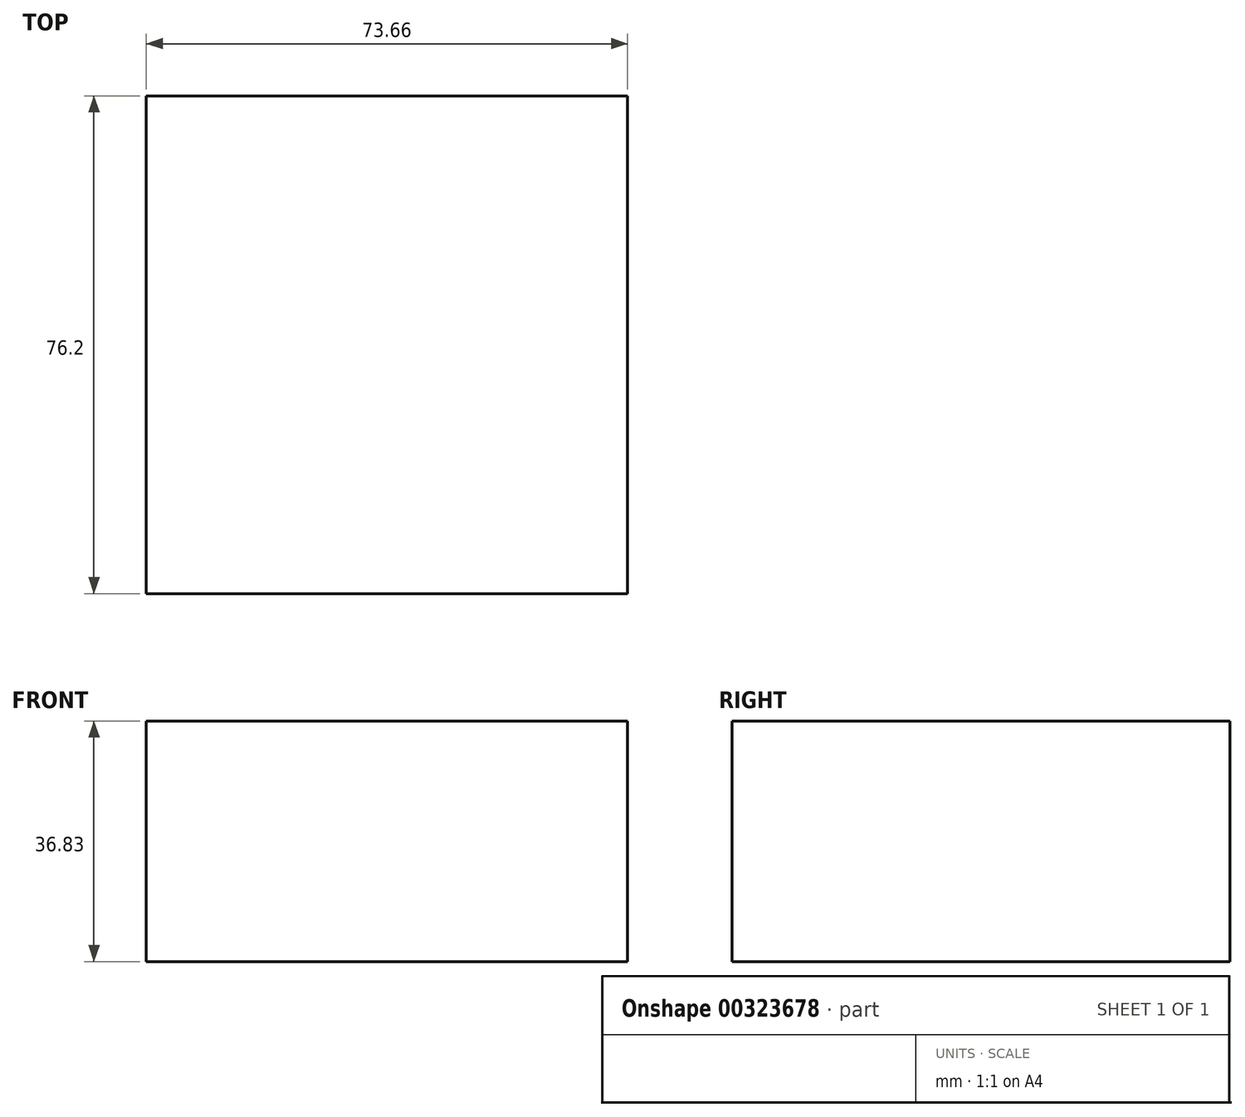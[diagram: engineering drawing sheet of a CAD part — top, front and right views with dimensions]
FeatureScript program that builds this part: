
annotation { "Feature Type Name" : "Feature", "Feature Type Description" : "" }
export const myFeature = defineFeature(function(context is Context, id is Id, definition is map)
    precondition{}
    {
        {
            var Q0;
            Q0=qCreatedBy(makeId("Front.planeOp"),FACE);
            var sketch = newSketch(context, id + "F0", { "sketchPlane" : qUnion([Q0])});
            skLineSegment(sketch, "E0.bottom", {"start": v(-38.8, 14.62) * mm, "end": v(34.86, 14.62) * mm});
            skLineSegment(sketch, "E0.top", {"start": v(-38.8, -22.21) * mm, "end": v(34.86, -22.21) * mm});
            skLineSegment(sketch, "E0.left", {"start": v(-38.8, 14.62) * mm, "end": v(-38.8, -22.21) * mm});
            skLineSegment(sketch, "E0.right", {"start": v(34.86, 14.62) * mm, "end": v(34.86, -22.21) * mm});
            skSolve(sketch);
        }
        {
            var Q0;
            Q0 = qSketchRegion(id + "F0", true);
            extrude(context, id + "F1", {"entities" : qUnion([Q0]), "depth" : 76.2 * mm});
        }
    });
